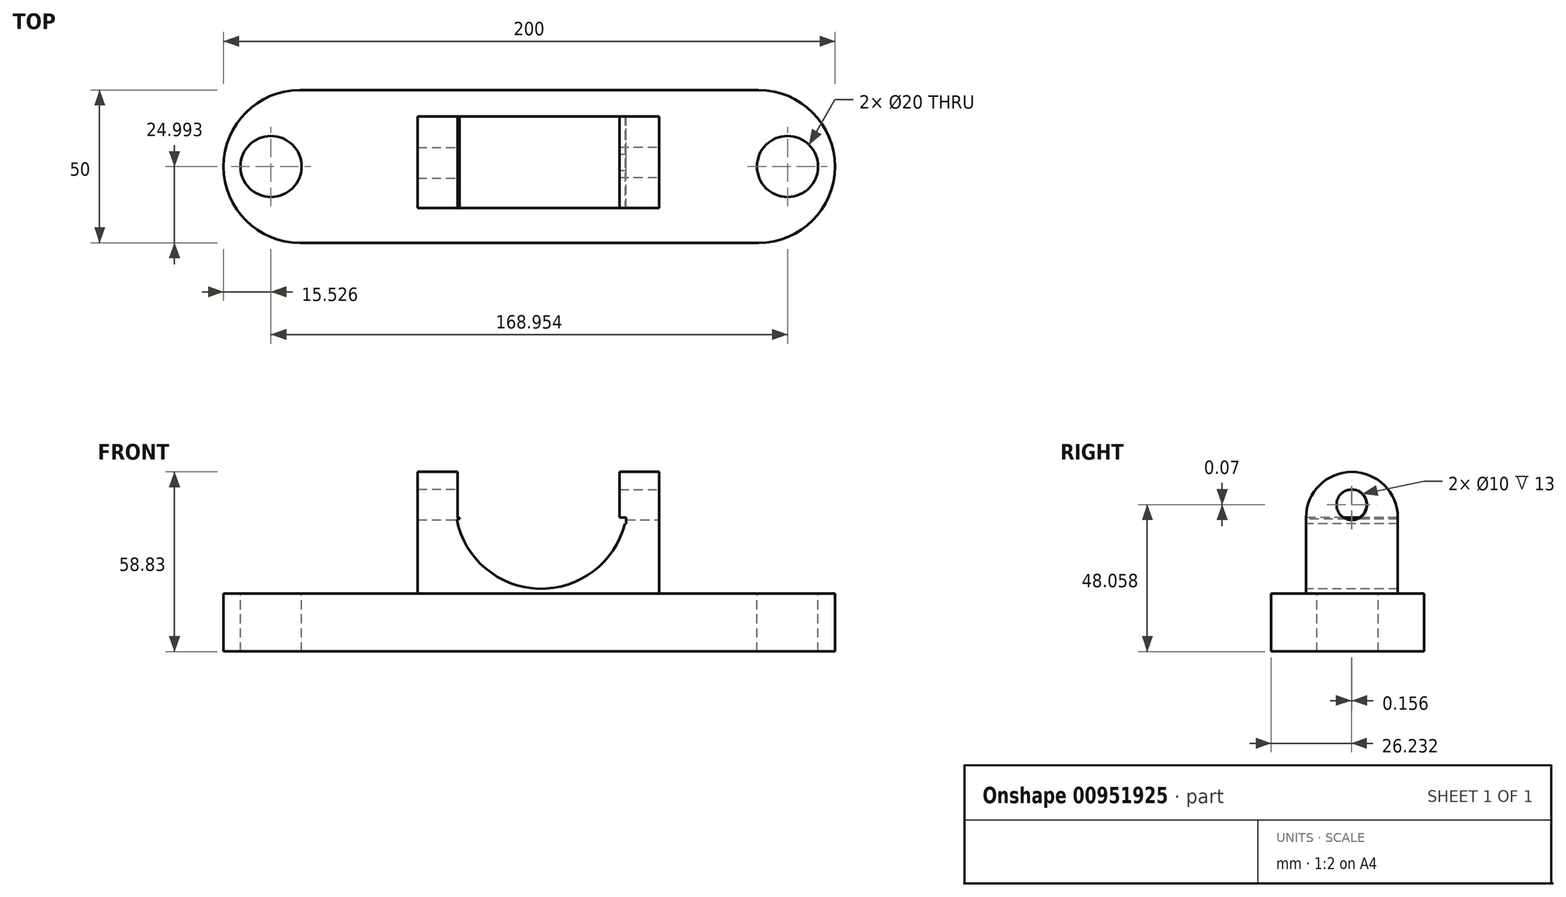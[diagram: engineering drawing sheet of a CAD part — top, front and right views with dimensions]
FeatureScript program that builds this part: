
annotation { "Feature Type Name" : "Feature", "Feature Type Description" : "" }
export const myFeature = defineFeature(function(context is Context, id is Id, definition is map)
    precondition{}
    {
        {
            var Q0;
            Q0=qCreatedBy(makeId("Front.planeOp"),FACE);
            var sketch = newSketch(context, id + "F0", { "sketchPlane" : qUnion([Q0])});
            skLineSegment(sketch, "E0.bottom", {"start": v(-75, -8.43) * mm, "end": v(75, -8.43) * mm});
            skLineSegment(sketch, "E0.top", {"start": v(-75, 10.57) * mm, "end": v(75, 10.57) * mm});
            skLineSegment(sketch, "E0.left", {"start": v(-75, -8.43) * mm, "end": v(-75, 10.57) * mm});
            skLineSegment(sketch, "E0.right", {"start": v(75, -8.43) * mm, "end": v(75, 10.57) * mm});
            skSolve(sketch);
        }
        {
            var Q0;
            Q0=makeQuery(id+"F0.imprint","IMPRINT",FACE,{"disambiguationData":[TD([[makeQuery(id+"F0.imprint","IMPRINT",EDGE,{"derivedFrom":sQuery(id+"F0.wireOp",EDGE,"E0.bottom")}),1.0]])]});
            extrude(context, id + "F1", {"entities" : qUnion([Q0]), "depth" : 50 * mm, "offsetDistance" : 25 * mm});
        }
        {
            var Q0;
            Q0=makeQuery(id+"F1.opExtrude","SWEPT_FACE",FACE,{"disambiguationData":[OSD([sQuery(id+"F0.wireOp",EDGE,"E0.top")])]});
            var sketch = newSketch(context, id + "F2", { "sketchPlane" : qUnion([Q0])});
            skArc(sketch, "E1", {"start": v(-75, 0) * mm, "mid": v(-100, -25) * mm, "end": v(-75, -50) * mm});
            skArc(sketch, "E2", {"start": v(75, -50) * mm, "mid": v(100, -25) * mm, "end": v(75, 0) * mm});
            skSolve(sketch);
        }
        {
            var Q0;
            Q0=makeQuery(id+"F2.imprint","IMPRINT",FACE,{"disambiguationData":[TD([[makeQuery(id+"F2.imprint","IMPRINT",EDGE,{"derivedFrom":sQuery(id+"F2.wireOp",EDGE,"E1")}),1.0]])]});
            var Q1;
            Q1=makeQuery(id+"F2.imprint","IMPRINT",FACE,{"disambiguationData":[TD([[makeQuery(id+"F2.imprint","IMPRINT",EDGE,{"derivedFrom":sQuery(id+"F2.wireOp",EDGE,"E2")}),1.0]])]});
            extrude(context, id + "F3", {"entities" : qUnion([Q0, Q1]), "operationType" : NewBodyOperationType.ADD, "oppositeDirection" : true, "depth" : 19 * mm, "offsetDistance" : 25 * mm});
        }
        {
            var Q0;
            Q0=qCreatedBy(makeId("Top.planeOp"),FACE);
            var sketch = newSketch(context, id + "F4", { "sketchPlane" : qUnion([Q0])});
            skLineSegment(sketch, "E3.bottom", {"start": v(-36.46, -8.59) * mm, "end": v(42.54, -8.59) * mm});
            skLineSegment(sketch, "E3.top", {"start": v(-36.46, -38.59) * mm, "end": v(42.54, -38.59) * mm});
            skLineSegment(sketch, "E3.left", {"start": v(-36.46, -8.59) * mm, "end": v(-36.46, -38.59) * mm});
            skLineSegment(sketch, "E3.right", {"start": v(42.54, -8.59) * mm, "end": v(42.54, -38.59) * mm});
            skSolve(sketch);
        }
        {
            var Q0;
            Q0 = qSketchRegion(id + "F4", true);
            extrude(context, id + "F5", {"entities" : qUnion([Q0]), "operationType" : NewBodyOperationType.ADD, "depth" : 35.4 * mm, "offsetDistance" : 25 * mm});
        }
        {
            var Q0;
            Q0=makeQuery(id+"F5.opExtrude","SWEPT_FACE",FACE,{"disambiguationData":[OSD([sQuery(id+"F4.wireOp",EDGE,"E3.top")])]});
            var sketch = newSketch(context, id + "F6", { "sketchPlane" : qUnion([Q0])});
            skSolve(sketch);
        }
        {
            var Q0;
            {var subQ0=sQuery(id+"F4.wireOp",EDGE,"E3.top");Q0=makeQuery(id+"F6.imprint","IMPRINT",FACE,{"disambiguationData":[TD([[makeQuery(id+"F6.imprint","IMPRINT",EDGE,{"derivedFrom":makeQuery(id+"F5.opExtrude","CAP_EDGE",EDGE,{"disambiguationData":[OSD([subQ0])],"isStart":false})}),-1.0]])]});}
            var sketch = newSketch(context, id + "F7", { "sketchPlane" : qUnion([Q0])});
            skArc(sketch, "E4", {"start": v(-23.75, 34.88) * mm, "mid": v(4.08, 12.13) * mm, "end": v(31.64, 35.21) * mm});
            skLineSegment(sketch, "E5", {"start": v(-23.75, 34.88) * mm, "end": v(31.64, 35.21) * mm});
            skSolve(sketch);
        }
        {
            var Q0;
            Q0 = qSketchRegion(id + "F7", true);
            extrude(context, id + "F8", {"entities" : qUnion([Q0]), "operationType" : NewBodyOperationType.REMOVE, "oppositeDirection" : true, "depth" : 30 * mm, "offsetDistance" : 25 * mm});
        }
        {
            var Q0;
            Q0=makeQuery(id+"F5.opExtrude","CAP_FACE",FACE,{"disambiguationData":[OSD([sQuery(id+"F4.wireOp",EDGE,"E3.bottom"),sQuery(id+"F4.wireOp",EDGE,"E3.top"),sQuery(id+"F4.wireOp",EDGE,"E3.left"),sQuery(id+"F4.wireOp",EDGE,"E3.right")])],"isStart":false});
            var sketch = newSketch(context, id + "F9", { "sketchPlane" : qUnion([Q0])});
            skLineSegment(sketch, "E6.bottom", {"start": v(-22.83, -38.59) * mm, "end": v(31.7, -38.59) * mm});
            skLineSegment(sketch, "E6.top", {"start": v(-22.83, -8.59) * mm, "end": v(31.7, -8.59) * mm});
            skLineSegment(sketch, "E6.left", {"start": v(-22.83, -38.59) * mm, "end": v(-22.83, -8.59) * mm});
            skLineSegment(sketch, "E6.right", {"start": v(31.7, -38.59) * mm, "end": v(31.7, -8.59) * mm});
            skSolve(sketch);
        }
        {
            var Q0;
            Q0 = qSketchRegion(id + "F9", true);
            extrude(context, id + "F10", {"entities" : qUnion([Q0]), "operationType" : NewBodyOperationType.REMOVE, "oppositeDirection" : true, "depth" : 2 * mm, "offsetDistance" : 25 * mm});
        }
        {
            var Q0;
            Q0=makeQuery(id+"F5.opExtrude","SWEPT_FACE",FACE,{"disambiguationData":[OSD([sQuery(id+"F4.wireOp",EDGE,"E3.left")])]});
            var sketch = newSketch(context, id + "F11", { "sketchPlane" : qUnion([Q0])});
            skArc(sketch, "E7", {"start": v(38.59, 35.4) * mm, "mid": v(23.59, 50.4) * mm, "end": v(8.59, 35.4) * mm});
            skSolve(sketch);
        }
        {
            var Q0;
            Q0 = qSketchRegion(id + "F11", true);
            var Q1;
            Q1=makeQuery(id+"F11.imprint","IMPRINT",FACE,{"disambiguationData":[TD([[makeQuery(id+"F11.imprint","IMPRINT",EDGE,{"derivedFrom":sQuery(id+"F11.wireOp",EDGE,"E7")}),1.0]])]});
            extrude(context, id + "F12", {"entities" : qUnion([Q0, Q1]), "operationType" : NewBodyOperationType.ADD, "oppositeDirection" : true, "depth" : 13 * mm, "offsetDistance" : 25 * mm});
        }
        {
            var Q0;
            Q0=makeQuery(id+"F5.opExtrude","SWEPT_FACE",FACE,{"disambiguationData":[OSD([sQuery(id+"F4.wireOp",EDGE,"E3.right")])]});
            var sketch = newSketch(context, id + "F13", { "sketchPlane" : qUnion([Q0])});
            skArc(sketch, "E8", {"start": v(-8.59, 35.4) * mm, "mid": v(-23.59, 50.4) * mm, "end": v(-38.59, 35.4) * mm});
            skSolve(sketch);
        }
        {
            var Q0;
            Q0 = qSketchRegion(id + "F13", true);
            var Q1;
            Q1=makeQuery(id+"F13.imprint","IMPRINT",FACE,{"disambiguationData":[TD([[makeQuery(id+"F13.imprint","IMPRINT",EDGE,{"derivedFrom":sQuery(id+"F13.wireOp",EDGE,"E8")}),1.0]])]});
            extrude(context, id + "F14", {"entities" : qUnion([Q0, Q1]), "operationType" : NewBodyOperationType.ADD, "oppositeDirection" : true, "depth" : 13 * mm, "offsetDistance" : 25 * mm});
        }
        {
            var Q0;
            {var subQ0=sQuery(id+"F4.wireOp",EDGE,"E3.right");Q0=makeQuery(id+"F14.boolean.opBoolean","MERGE",FACE,{"derivedFrom":[makeQuery(id+"F5.opExtrude","SWEPT_FACE",FACE,{"disambiguationData":[OSD([subQ0])]}),makeQuery(id+"F14.opExtrude","CAP_FACE",FACE,{"disambiguationData":[OSD([subQ0,sQuery(id+"F13.wireOp",EDGE,"E8")])],"isStart":true})]});}
            var sketch = newSketch(context, id + "F15", { "sketchPlane" : qUnion([Q0])});
            skCircle(sketch, "E9", {"center": v(-23.61, 39.63) * mm, "radius": 5 * mm});
            skSolve(sketch);
        }
        {
            var Q0;
            Q0 = qSketchRegion(id + "F15", true);
            extrude(context, id + "F16", {"entities" : qUnion([Q0]), "operationType" : NewBodyOperationType.REMOVE, "oppositeDirection" : true, "depth" : 13 * mm, "offsetDistance" : 25 * mm});
        }
        {
            var Q0;
            Q0=makeQuery(id+"F12.opExtrude","CAP_FACE",FACE,{"disambiguationData":[OSD([sQuery(id+"F4.wireOp",EDGE,"E3.left"),sQuery(id+"F11.wireOp",EDGE,"E7")])],"isStart":false});
            var sketch = newSketch(context, id + "F17", { "sketchPlane" : qUnion([Q0])});
            skCircle(sketch, "E10", {"center": v(-23.77, 39.7) * mm, "radius": 5 * mm});
            skSolve(sketch);
        }
        {
            var Q0;
            {var subQ0=sQuery(id+"F17.wireOp",EDGE,"E10");var subQ1=makeQuery(id+"F12.opExtrude","CAP_EDGE",EDGE,{"disambiguationData":[OSD([sQuery(id+"F4.wireOp",EDGE,"E3.left")])],"isStart":false});var subQ2=makeQuery(id+"F17.imprint","INTERSECT",VERTEX,{"disambiguationData":[OD(0.0)],"derivedFrom":[subQ1,subQ0]});Q0=makeQuery(id+"F17.imprint","IMPRINT",FACE,{"disambiguationData":[TD([[makeQuery(id+"F17.imprint","IMPRINT",EDGE,{"disambiguationData":[TD([[subQ2,1.0]])],"derivedFrom":subQ0}),1.0]])]});}
            var Q1;
            {var subQ0=sQuery(id+"F17.wireOp",EDGE,"E10");var subQ1=makeQuery(id+"F12.opExtrude","CAP_EDGE",EDGE,{"disambiguationData":[OSD([sQuery(id+"F4.wireOp",EDGE,"E3.left")])],"isStart":false});var subQ2=makeQuery(id+"F17.imprint","INTERSECT",VERTEX,{"disambiguationData":[OD(0.0)],"derivedFrom":[subQ1,subQ0]});Q1=makeQuery(id+"F17.imprint","IMPRINT",FACE,{"disambiguationData":[TD([[makeQuery(id+"F17.imprint","IMPRINT",EDGE,{"disambiguationData":[TD([[subQ2,-1.0]])],"derivedFrom":subQ0}),1.0]])]});}
            extrude(context, id + "F18", {"entities" : qUnion([Q0, Q1]), "operationType" : NewBodyOperationType.REMOVE, "oppositeDirection" : true, "depth" : 13 * mm, "offsetDistance" : 25 * mm});
        }
        {
            var Q0;
            {var subQ0=sQuery(id+"F0.wireOp",EDGE,"E0.top");Q0=makeQuery(id+"F3.boolean.opBoolean","MERGE",FACE,{"derivedFrom":[makeQuery(id+"F1.opExtrude","SWEPT_FACE",FACE,{"disambiguationData":[OSD([subQ0])]}),makeQuery(id+"F3.opExtrude","CAP_FACE",FACE,{"disambiguationData":[OSD([subQ0,sQuery(id+"F0.wireOp",EDGE,"E0.left"),sQuery(id+"F2.wireOp",EDGE,"E1")])],"isStart":true}),makeQuery(id+"F3.opExtrude","CAP_FACE",FACE,{"disambiguationData":[OSD([subQ0,sQuery(id+"F0.wireOp",EDGE,"E0.right"),sQuery(id+"F2.wireOp",EDGE,"E2")])],"isStart":true})]});}
            var sketch = newSketch(context, id + "F19", { "sketchPlane" : qUnion([Q0])});
            skCircle(sketch, "E11", {"center": v(-84.47, -25) * mm, "radius": 10 * mm});
            skCircle(sketch, "E12", {"center": v(84.48, -25) * mm, "radius": 10 * mm});
            skSolve(sketch);
        }
        {
            var Q0;
            Q0=makeQuery(id+"F19.imprint","IMPRINT",FACE,{"disambiguationData":[TD([[makeQuery(id+"F19.imprint","IMPRINT",EDGE,{"derivedFrom":sQuery(id+"F19.wireOp",EDGE,"E11")}),1.0]])]});
            extrude(context, id + "F20", {"entities" : qUnion([Q0]), "operationType" : NewBodyOperationType.REMOVE, "oppositeDirection" : true, "depth" : 19 * mm, "offsetDistance" : 25 * mm});
        }
        {
            var Q0;
            Q0 = qSketchRegion(id + "F19", true);
            extrude(context, id + "F21", {"entities" : qUnion([Q0]), "operationType" : NewBodyOperationType.REMOVE, "oppositeDirection" : true, "depth" : 19 * mm, "offsetDistance" : 25 * mm});
        }
    });
